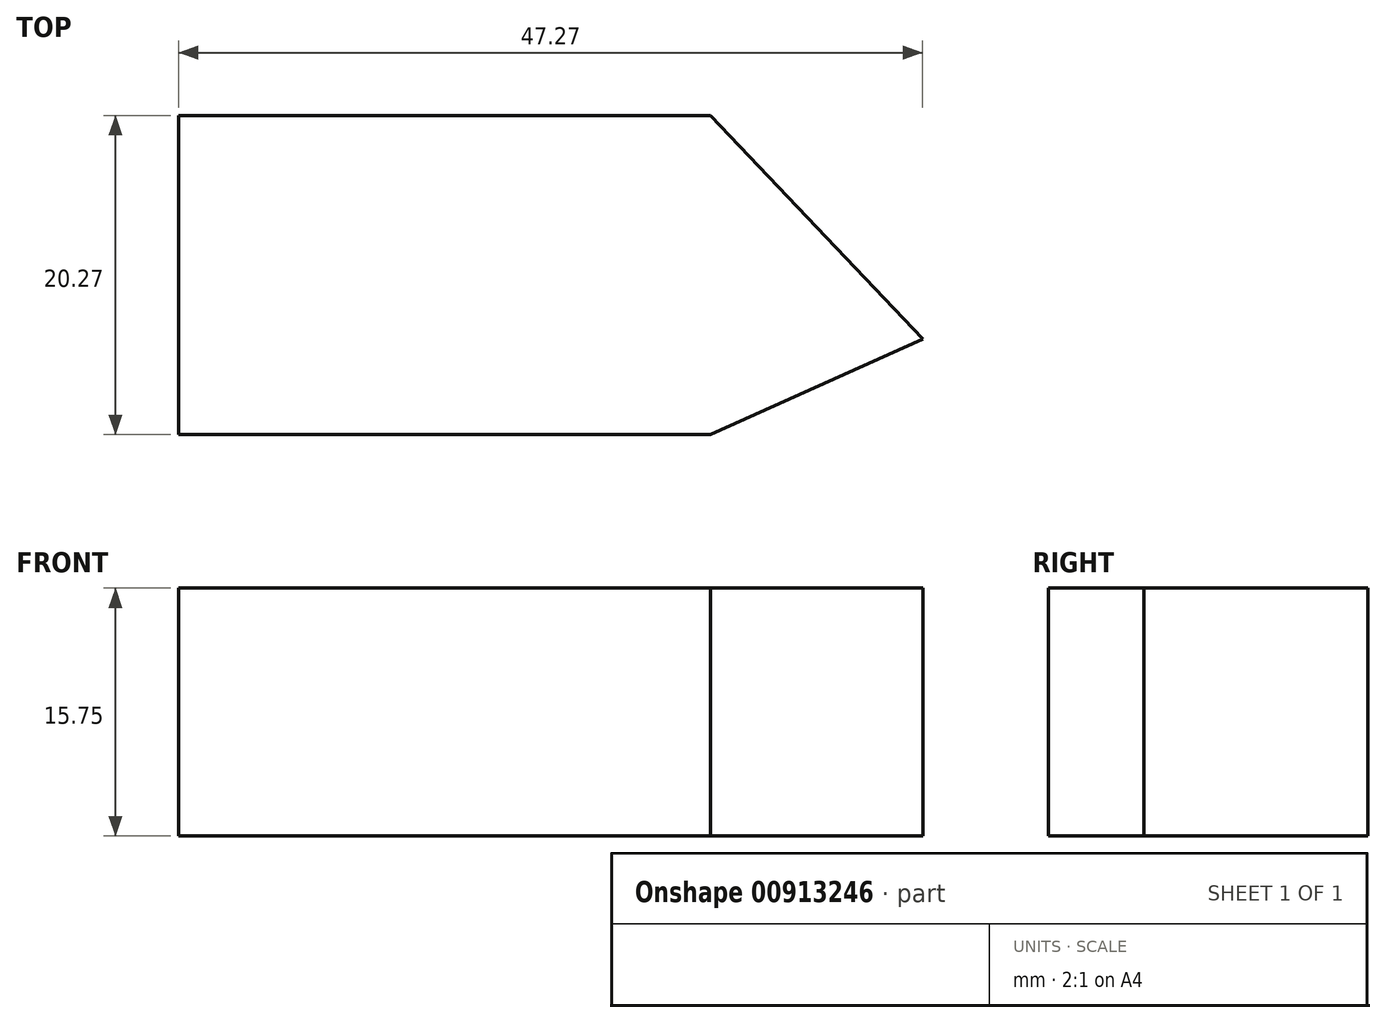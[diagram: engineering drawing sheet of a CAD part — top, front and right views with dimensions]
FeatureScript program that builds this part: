
annotation { "Feature Type Name" : "Feature", "Feature Type Description" : "" }
export const myFeature = defineFeature(function(context is Context, id is Id, definition is map)
    precondition{}
    {
        {
            var Q0;
            Q0=qCreatedBy(makeId("Top.planeOp"),FACE);
            var sketch = newSketch(context, id + "F0", { "sketchPlane" : qUnion([Q0])});
            skLineSegment(sketch, "E0", {"start": v(-52.46, 14.2) * mm, "end": v(-18.66, 14.2) * mm});
            skLineSegment(sketch, "E1", {"start": v(-18.66, 14.2) * mm, "end": v(-5.19, 0) * mm});
            skLineSegment(sketch, "E2", {"start": v(-5.19, 0) * mm, "end": v(-18.66, -6.06) * mm});
            skLineSegment(sketch, "E3", {"start": v(-18.66, -6.06) * mm, "end": v(-52.46, -6.06) * mm});
            skLineSegment(sketch, "E4", {"start": v(-52.46, -6.06) * mm, "end": v(-52.46, 14.2) * mm});
            skSolve(sketch);
        }
        {
            var Q0;
            Q0=makeQuery(id+"F0.imprint","IMPRINT",FACE,{"disambiguationData":[TD([[makeQuery(id+"F0.imprint","IMPRINT",EDGE,{"derivedFrom":sQuery(id+"F0.wireOp",EDGE,"E0")}),-1.0]])]});
            extrude(context, id + "F1", {"entities" : qUnion([Q0]), "depth" : 15.75 * mm, "offsetDistance" : 25.4 * mm});
        }
    });
